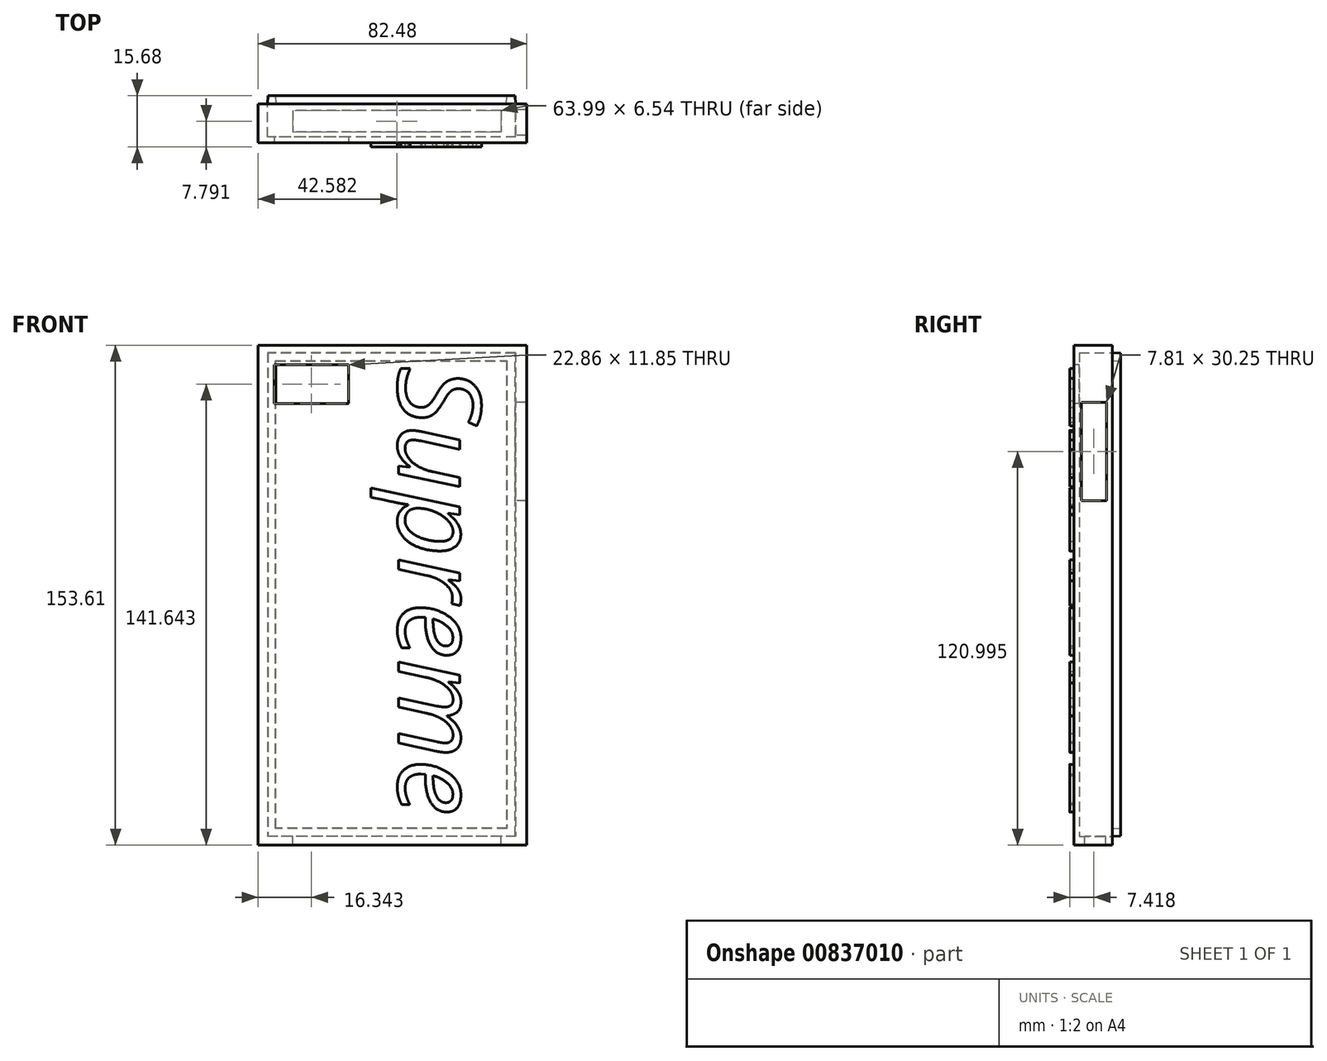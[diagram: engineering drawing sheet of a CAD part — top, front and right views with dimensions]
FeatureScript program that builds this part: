
annotation { "Feature Type Name" : "Feature", "Feature Type Description" : "" }
export const myFeature = defineFeature(function(context is Context, id is Id, definition is map)
    precondition{}
    {
        {
            var Q0;
            Q0=qCreatedBy(makeId("Front.planeOp"),FACE);
            var sketch = newSketch(context, id + "F0", { "sketchPlane" : qUnion([Q0])});
            skLineSegment(sketch, "E0.bottom", {"start": v(-45.35, 72.92) * mm, "end": v(37.13, 72.92) * mm});
            skLineSegment(sketch, "E0.top", {"start": v(-45.35, -80.69) * mm, "end": v(37.13, -80.69) * mm});
            skLineSegment(sketch, "E0.left", {"start": v(-45.35, 72.92) * mm, "end": v(-45.35, -80.69) * mm});
            skLineSegment(sketch, "E0.right", {"start": v(37.13, 72.92) * mm, "end": v(37.13, -80.69) * mm});
            skLineSegment(sketch, "E1.bottom", {"start": v(-40.44, 66.88) * mm, "end": v(-17.58, 66.88) * mm});
            skLineSegment(sketch, "E1.top", {"start": v(-40.44, 55.03) * mm, "end": v(-17.58, 55.03) * mm});
            skLineSegment(sketch, "E1.left", {"start": v(-40.44, 66.88) * mm, "end": v(-40.44, 55.03) * mm});
            skLineSegment(sketch, "E1.right", {"start": v(-17.58, 66.88) * mm, "end": v(-17.58, 55.03) * mm});
            skSolve(sketch);
        }
        {
            var Q0;
            Q0=qCreatedBy(makeId("Front.planeOp"),FACE);
            var sketch = newSketch(context, id + "F1", { "sketchPlane" : qUnion([Q0])});
            skText(sketch, "E2", { "text": "Supreme", "fontName": "OpenSans-Italic.ttf"});
            const initialGuessF1  = {"E2": [-0.00229, 0.0664, 0, -1, 0.0254]};
            skSetInitialGuess(sketch, initialGuessF1);
            skSolve(sketch);
        }
        {
            var Q0;
            Q0=makeQuery(id+"F0.imprint","IMPRINT",FACE,{"disambiguationData":[TD([[makeQuery(id+"F0.imprint","IMPRINT",EDGE,{"derivedFrom":sQuery(id+"F0.wireOp",EDGE,"E0.bottom")}),-1.0]])]});
            extrude(context, id + "F2", {"entities" : qUnion([Q0]), "oppositeDirection" : true, "depth" : 11.87 * mm, "offsetDistance" : 25.4 * mm});
        }
        {
            var Q0;
            Q0 = qSketchRegion(id + "F1", true);
            extrude(context, id + "F3", {"entities" : qUnion([Q0]), "operationType" : NewBodyOperationType.ADD, "depth" : 1.27 * mm, "offsetDistance" : 25.4 * mm});
        }
        {
            var Q0;
            Q0=qCreatedBy(makeId("Front.planeOp"),FACE);
            cPlane(context, id + "F4", {"entities" : qUnion([Q0]), "cplaneType" : CPlaneType.OFFSET, "offset" : 11.87 * mm, "oppositeDirection" : true, "width" : 152.4 * mm, "height" : 152.4 * mm});
        }
        {
            var Q0;
            Q0=qCreatedBy(id+"F4.planeOp",FACE);
            var sketch = newSketch(context, id + "F5", { "sketchPlane" : qUnion([Q0])});
            skLineSegment(sketch, "E3.bottom", {"start": v(33.73, 70.65) * mm, "end": v(-42.47, 70.65) * mm});
            skLineSegment(sketch, "E3.top", {"start": v(33.73, -77.94) * mm, "end": v(-42.47, -77.94) * mm});
            skLineSegment(sketch, "E3.left", {"start": v(33.73, 70.65) * mm, "end": v(33.73, -77.94) * mm});
            skLineSegment(sketch, "E3.right", {"start": v(-42.47, 70.65) * mm, "end": v(-42.47, -77.94) * mm});
            skSolve(sketch);
        }
        {
            var Q0;
            Q0=makeQuery(id+"F5.imprint","IMPRINT",FACE,{"disambiguationData":[TD([[makeQuery(id+"F5.imprint","IMPRINT",EDGE,{"derivedFrom":sQuery(id+"F5.wireOp",EDGE,"E3.bottom")}),1.0]])]});
            extrude(context, id + "F6", {"entities" : qUnion([Q0]), "operationType" : NewBodyOperationType.REMOVE, "depth" : 10.16 * mm, "offsetDistance" : 25.4 * mm});
        }
        {
            var Q0;
            Q0=qCreatedBy(id+"F4.planeOp",FACE);
            var sketch = newSketch(context, id + "F7", { "sketchPlane" : qUnion([Q0])});
            skLineSegment(sketch, "E4", {"start": v(33.73, 70.65) * mm, "end": v(30.95, 70.65) * mm});
            skLineSegment(sketch, "E5", {"start": v(30.95, 70.65) * mm, "end": v(30.95, -77.94) * mm});
            skLineSegment(sketch, "E6", {"start": v(30.95, -77.94) * mm, "end": v(33.73, -77.94) * mm});
            skLineSegment(sketch, "E7", {"start": v(33.73, -77.94) * mm, "end": v(33.73, 70.65) * mm});
            skLineSegment(sketch, "E8", {"start": v(30.95, 70.65) * mm, "end": v(30.95, 68.12) * mm});
            skLineSegment(sketch, "E9", {"start": v(30.95, 68.12) * mm, "end": v(-42.47, 68.12) * mm});
            skLineSegment(sketch, "E10", {"start": v(-42.47, 68.12) * mm, "end": v(-42.47, 70.65) * mm});
            skLineSegment(sketch, "E11", {"start": v(-42.47, 70.65) * mm, "end": v(30.95, 70.65) * mm});
            skLineSegment(sketch, "E12", {"start": v(-42.47, 68.12) * mm, "end": v(-39.92, 68.12) * mm});
            skLineSegment(sketch, "E13", {"start": v(-39.92, 68.12) * mm, "end": v(-39.92, -77.94) * mm});
            skLineSegment(sketch, "E14", {"start": v(-39.92, -77.94) * mm, "end": v(-42.47, -77.94) * mm});
            skLineSegment(sketch, "E15", {"start": v(-42.47, -77.94) * mm, "end": v(-42.47, 68.12) * mm});
            skLineSegment(sketch, "E16", {"start": v(-39.92, -77.94) * mm, "end": v(-39.92, -75.39) * mm});
            skLineSegment(sketch, "E17", {"start": v(-39.92, -75.39) * mm, "end": v(30.95, -75.39) * mm});
            skLineSegment(sketch, "E18", {"start": v(30.95, -75.39) * mm, "end": v(30.95, -77.94) * mm});
            skLineSegment(sketch, "E19", {"start": v(-39.92, -77.94) * mm, "end": v(30.95, -77.94) * mm});
            skSolve(sketch);
        }
        {
            var Q0;
            Q0 = qSketchRegion(id + "F7", true);
            extrude(context, id + "F8", {"entities" : qUnion([Q0]), "oppositeDirection" : true, "depth" : 2.54 * mm, "offsetDistance" : 25.4 * mm, "hasDraft" : true, "draftAngle" : 3 * degree, "draftPullDirection" : true});
        }
        {
            var Q0;
            Q0=qCreatedBy(makeId("Top.planeOp"),FACE);
            var sketch = newSketch(context, id + "F9", { "sketchPlane" : qUnion([Q0])});
            skLineSegment(sketch, "E20.bottom", {"start": v(-34.76, 3.25) * mm, "end": v(29.23, 3.25) * mm});
            skLineSegment(sketch, "E20.top", {"start": v(-34.76, 9.8) * mm, "end": v(29.23, 9.8) * mm});
            skLineSegment(sketch, "E20.left", {"start": v(-34.76, 3.25) * mm, "end": v(-34.76, 9.8) * mm});
            skLineSegment(sketch, "E20.right", {"start": v(29.23, 3.25) * mm, "end": v(29.23, 9.8) * mm});
            skSolve(sketch);
        }
        {
            var Q0;
            Q0 = qSketchRegion(id + "F9", true);
            extrude(context, id + "F10", {"entities" : qUnion([Q0]), "operationType" : NewBodyOperationType.REMOVE, "oppositeDirection" : true, "depth" : 127 * mm, "offsetDistance" : 25.4 * mm});
        }
        {
            var Q0;
            Q0=qCreatedBy(makeId("Right.planeOp"),FACE);
            var sketch = newSketch(context, id + "F11", { "sketchPlane" : qUnion([Q0])});
            skLineSegment(sketch, "E21.bottom", {"start": v(2.24, 55.43) * mm, "end": v(10.05, 55.43) * mm});
            skLineSegment(sketch, "E21.top", {"start": v(2.24, 25.18) * mm, "end": v(10.05, 25.18) * mm});
            skLineSegment(sketch, "E21.left", {"start": v(2.24, 55.43) * mm, "end": v(2.24, 25.18) * mm});
            skLineSegment(sketch, "E21.right", {"start": v(10.05, 55.43) * mm, "end": v(10.05, 25.18) * mm});
            skSolve(sketch);
        }
        {
            var Q0;
            Q0 = qSketchRegion(id + "F11", true);
            extrude(context, id + "F12", {"entities" : qUnion([Q0]), "operationType" : NewBodyOperationType.REMOVE, "depth" : 101.6 * mm, "offsetDistance" : 25.4 * mm});
        }
    });
